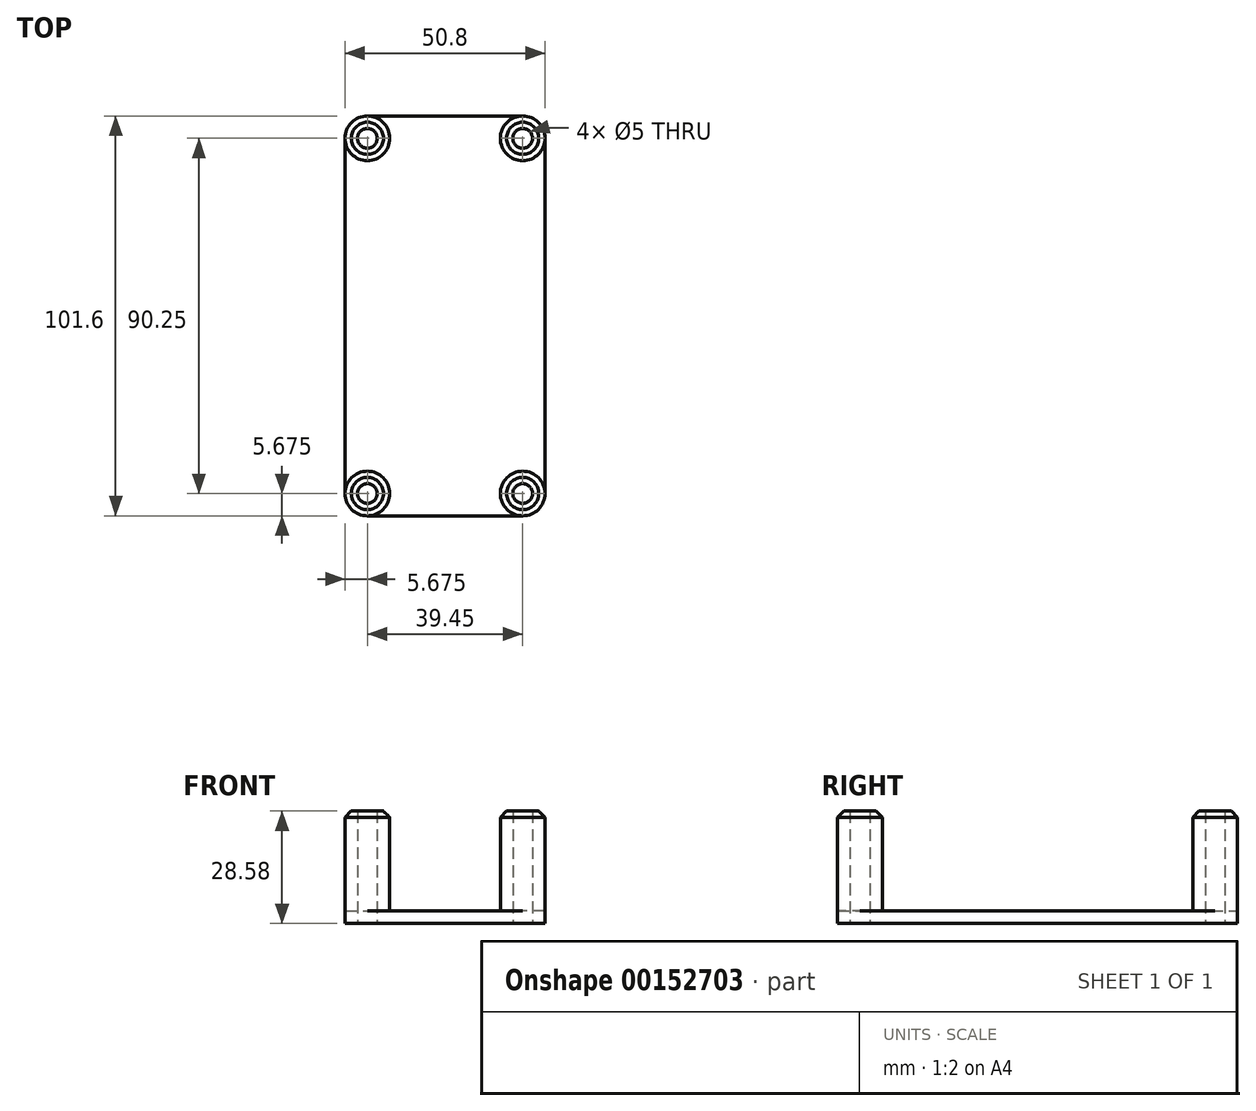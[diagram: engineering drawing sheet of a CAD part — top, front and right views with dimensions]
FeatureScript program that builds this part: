
annotation { "Feature Type Name" : "Feature", "Feature Type Description" : "" }
export const myFeature = defineFeature(function(context is Context, id is Id, definition is map)
    precondition{}
    {
        {
            var Q0;
            Q0=qCreatedBy(makeId("Top.planeOp"),FACE);
            var sketch = newSketch(context, id + "F0", { "sketchPlane" : qUnion([Q0])});
            skLineSegment(sketch, "E0.bottom", {"start": v(19.73, 45.13) * mm, "end": v(-19.73, 45.13) * mm, "construction": true});
            skLineSegment(sketch, "E0.top", {"start": v(19.73, -45.13) * mm, "end": v(-19.73, -45.13) * mm, "construction": true});
            skLineSegment(sketch, "E0.left", {"start": v(19.72, 45.12) * mm, "end": v(19.73, -45.13) * mm, "construction": true});
            skLineSegment(sketch, "E0.right", {"start": v(-19.73, 45.12) * mm, "end": v(-19.73, -45.13) * mm, "construction": true});
            skPoint(sketch, "E0.middle", {"position": v(0, 0) * mm});
            skLineSegment(sketch, "E1.bottom", {"start": v(25.4, 50.8) * mm, "end": v(-25.4, 50.8) * mm});
            skLineSegment(sketch, "E1.top", {"start": v(25.4, -50.8) * mm, "end": v(-25.4, -50.8) * mm});
            skLineSegment(sketch, "E1.left", {"start": v(25.4, 50.8) * mm, "end": v(25.4, -50.8) * mm});
            skLineSegment(sketch, "E1.right", {"start": v(-25.4, 50.8) * mm, "end": v(-25.4, -50.8) * mm});
            skLineSegment(sketch, "E2", {"start": v(19.73, 45.12) * mm, "end": v(19.73, 50.8) * mm, "construction": true});
            skLineSegment(sketch, "E3", {"start": v(19.73, 45.13) * mm, "end": v(25.4, 45.13) * mm, "construction": true});
            skCircle(sketch, "E4", {"center": v(-19.73, 45.12) * mm, "radius": 2.5 * mm});
            skCircle(sketch, "E5", {"center": v(19.73, 45.12) * mm, "radius": 2.5 * mm});
            skCircle(sketch, "E6", {"center": v(19.73, -45.13) * mm, "radius": 2.5 * mm});
            skCircle(sketch, "E7", {"center": v(-19.73, -45.13) * mm, "radius": 2.5 * mm});
            skSolve(sketch);
        }
        {
            var Q0;
            Q0 = qSketchRegion(id + "F0", true);
            extrude(context, id + "F1", {"entities" : qUnion([Q0]), "depth" : 3.17 * mm});
        }
        {
            var Q0;
            Q0=makeQuery(id+"F1.opExtrude","SWEPT_EDGE",EDGE,{"disambiguationData":[OSD([sQuery(id+"F0.wireOp",EDGE,"E1.bottom"),sQuery(id+"F0.wireOp",EDGE,"E1.left")])]});
            var Q1;
            Q1=makeQuery(id+"F1.opExtrude","SWEPT_EDGE",EDGE,{"disambiguationData":[OSD([sQuery(id+"F0.wireOp",EDGE,"E1.bottom"),sQuery(id+"F0.wireOp",EDGE,"E1.right")])]});
            var Q2;
            Q2=makeQuery(id+"F1.opExtrude","SWEPT_EDGE",EDGE,{"disambiguationData":[OSD([sQuery(id+"F0.wireOp",EDGE,"E1.top"),sQuery(id+"F0.wireOp",EDGE,"E1.right")])]});
            var Q3;
            Q3=makeQuery(id+"F1.opExtrude","SWEPT_EDGE",EDGE,{"disambiguationData":[OSD([sQuery(id+"F0.wireOp",EDGE,"E1.top"),sQuery(id+"F0.wireOp",EDGE,"E1.left")])]});
            fillet(context, id + "F2", {"entities" : qUnion([Q0, Q1, Q2, Q3]), "radius" : 5.67 * mm, "tangentPropagation" : true, "allowEdgeOverflow" : false});
        }
        {
            var Q0;
            Q0=makeQuery(id+"F1.opExtrude","CAP_FACE",FACE,{"disambiguationData":[OSD([sQuery(id+"F0.wireOp",EDGE,"E1.bottom"),sQuery(id+"F0.wireOp",EDGE,"E1.top"),sQuery(id+"F0.wireOp",EDGE,"E1.left"),sQuery(id+"F0.wireOp",EDGE,"E1.right"),sQuery(id+"F0.wireOp",EDGE,"E4"),sQuery(id+"F0.wireOp",EDGE,"E5"),sQuery(id+"F0.wireOp",EDGE,"E6"),sQuery(id+"F0.wireOp",EDGE,"E7")])],"isStart":false});
            var sketch = newSketch(context, id + "F3", { "sketchPlane" : qUnion([Q0])});
            skCircle(sketch, "E8", {"center": v(19.73, 45.12) * mm, "radius": 2.5 * mm});
            skCircle(sketch, "E9", {"center": v(19.73, 45.13) * mm, "radius": 5.67 * mm});
            skCircle(sketch, "E10", {"center": v(19.73, -45.13) * mm, "radius": 2.5 * mm});
            skCircle(sketch, "E11", {"center": v(19.73, -45.13) * mm, "radius": 5.67 * mm});
            skCircle(sketch, "E12", {"center": v(-19.73, -45.13) * mm, "radius": 5.67 * mm});
            skCircle(sketch, "E13", {"center": v(-19.73, -45.13) * mm, "radius": 2.5 * mm});
            skCircle(sketch, "E14", {"center": v(-19.73, 45.12) * mm, "radius": 2.5 * mm});
            skCircle(sketch, "E15", {"center": v(-19.73, 45.13) * mm, "radius": 5.67 * mm});
            skSolve(sketch);
        }
        {
            var Q0;
            Q0 = qSketchRegion(id + "F3", true);
            extrude(context, id + "F4", {"entities" : qUnion([Q0]), "operationType" : NewBodyOperationType.ADD, "depth" : 25.4 * mm});
        }
        {
            var Q0;
            Q0=makeQuery(id+"F4.opExtrude","CAP_EDGE",EDGE,{"disambiguationData":[OSD([sQuery(id+"F3.wireOp",EDGE,"E9")])],"isStart":false});
            var Q1;
            Q1=makeQuery(id+"F4.opExtrude","CAP_EDGE",EDGE,{"disambiguationData":[OSD([sQuery(id+"F3.wireOp",EDGE,"E15")])],"isStart":false});
            var Q2;
            Q2=makeQuery(id+"F4.opExtrude","CAP_EDGE",EDGE,{"disambiguationData":[OSD([sQuery(id+"F3.wireOp",EDGE,"E12")])],"isStart":false});
            var Q3;
            Q3=makeQuery(id+"F4.opExtrude","CAP_EDGE",EDGE,{"disambiguationData":[OSD([sQuery(id+"F3.wireOp",EDGE,"E11")])],"isStart":false});
            var Q4;
            Q4=makeQuery(id+"F4.opExtrude","CAP_EDGE",EDGE,{"disambiguationData":[OSD([sQuery(id+"F3.wireOp",EDGE,"E11")])],"isStart":true});
            var Q5;
            Q5=makeQuery(id+"F4.opExtrude","CAP_EDGE",EDGE,{"disambiguationData":[OSD([sQuery(id+"F3.wireOp",EDGE,"E12")])],"isStart":true});
            var Q6;
            Q6=makeQuery(id+"F4.opExtrude","CAP_EDGE",EDGE,{"disambiguationData":[OSD([sQuery(id+"F3.wireOp",EDGE,"E15")])],"isStart":true});
            var Q7;
            Q7=makeQuery(id+"F4.opExtrude","CAP_EDGE",EDGE,{"disambiguationData":[OSD([sQuery(id+"F3.wireOp",EDGE,"E9")])],"isStart":true});
            chamfer(context, id + "F5", {"entities" : qUnion([Q0, Q1, Q2, Q3, Q4, Q5, Q6, Q7]), "width" : 1.59 * mm, "tangentPropagation" : true});
        }
    });
